# Revit family: 3079108 Feilo Sylvania Lighting Fixture CLIO 430 LED 3000K
name_source: partatom
category: Lighting Fixtures
revit_build: Autodesk Revit 2017 (Build: 20190507_1515(x64)
units: mm (PartAtom-declared; Revit-internal decimal feet)

## family parameters
Cut with Voids When Loaded = No
Host = Face
Light Source = Yes
OmniClass Number = 23.80.70.11.17
OmniClass Title = Specialized Lighting by Location or Use
Part Type = Normal
Room Calculation Point = No
Round Connector Dimension = Use Diameter
Shared = No

## types (1)
- 3079108 CLIO 430 LED 3000K
    Apparent Load = 26 VA
    Assembly Code = D5020200
    AssetType = Fixed
    Color Filter = 16777215
    Default Elevation = 0 mm  [stored 0 ft]
    Description = Large ambient bulkhead luminaire with indirect halo effect, loop in/loop out wiring, surface or rear cable entry, white polycarbonate housing with opal diffuser, 2076lm, 25W, 83lm/W, 3000K, 640mA, 80CRI, non-dimmable, IP44, IK06, 40,000 hours (L70), Ø430x132mm, 5 SDCM, 1.7kg, Class II, 220-240V, Energy class A++ (integrated LED)
    Diameter_FEILO = 430 mm
    Dimming Lamp Color Temperature Shift = <None>
    DocumentationLiterature = http://www.sylvania-lighting.com
    DurationUnit = hours
    ElectricShockClassification = Class II
    ExpectedLife = 50000
    Height_FEILO = 132 mm
    IfcExportAs = IfcLightFixtureType
    IfcExportType = IfcLightFixtureType
    ImpactProtectionIndex = IK06
    IngressProtection = IP44
    InputNominalFrequency = 50/60 Hz
    InputVoltage = 220-240V~
    Keynote = 16500
    Lamp = 20W
    LampColourRenderingIndex = 80
    LampColourTemperature = 3000 K
    LampNominalLuminous = 2000 lm
    LampsType = 20W
    LuminousEfficacy = 76.92 lm/W
    Manufacturer = Feilo Sylvania
    ManufacturerName = Feilo Sylvania
    Material_1_FEILO = Polycarbonate_Sylvania_Clio LED_White
    Material_2_FEILO = Acrylic Glass_Sylvania_Clio LED_White
    Material_3_FEILO = <By Category>
    Material_4_FEILO = <By Category>
    Model = CLIO 430 LED 3000K
    ModelNumber = 3079108
    ModelReference = CLIO 430 LED 3000K
    Name = CLIO 430 LED 3000K
    NominalHeight = 134.5 mm
    NominalLength = 430 mm
    NominalWidth = 0 mm  [stored 0 ft]
    Photometric Web File = 3079108.ies
    PowerConsumption = 26 W
    PowerFactor = 0
    Radius_FEILO = 215 mm
    Tilt Angle = -90.00°
    TypeName = CLIO 430 LED 3000K
    URL = http://www.sylvania-lighting.com
    Voltage = 230 V
    Weight = 1.69 kg

note: [stored X ft] marks values corroborated as IEEE doubles in the binary element streams (Revit-internal decimal feet)

## geometry (parser evidence)
native form markers: Sweep x3
no freeform markers — native parametric forms only
